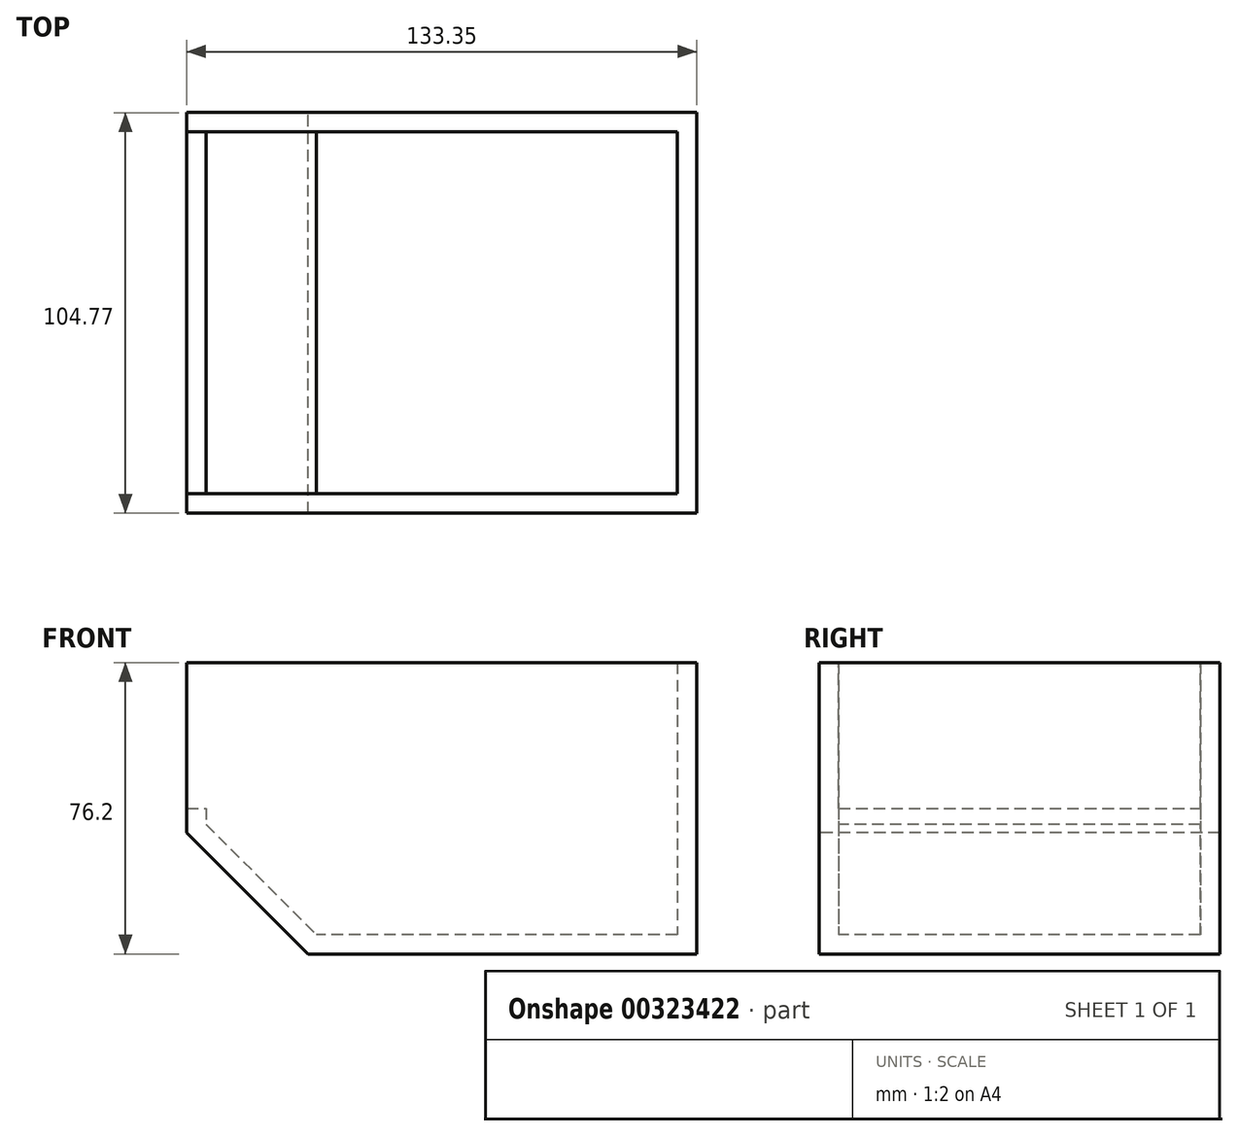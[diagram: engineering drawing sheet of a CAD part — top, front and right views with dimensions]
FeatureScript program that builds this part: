
annotation { "Feature Type Name" : "Feature", "Feature Type Description" : "" }
export const myFeature = defineFeature(function(context is Context, id is Id, definition is map)
    precondition{}
    {
        {
            var Q0;
            Q0=qCreatedBy(makeId("Top.planeOp"),FACE);
            var sketch = newSketch(context, id + "F0", { "sketchPlane" : qUnion([Q0])});
            skLineSegment(sketch, "E0", {"start": v(0, 0) * mm, "end": v(0, 104.78) * mm});
            skLineSegment(sketch, "E1", {"start": v(0, 104.78) * mm, "end": v(133.35, 104.78) * mm});
            skLineSegment(sketch, "E2", {"start": v(133.35, 104.78) * mm, "end": v(133.35, 0) * mm});
            skLineSegment(sketch, "E3", {"start": v(133.35, 0) * mm, "end": v(0, 0) * mm});
            skSolve(sketch);
        }
        {
            var Q0;
            Q0=makeQuery(id+"F0.imprint","IMPRINT",FACE,{"disambiguationData":[TD([[makeQuery(id+"F0.imprint","IMPRINT",EDGE,{"derivedFrom":sQuery(id+"F0.wireOp",EDGE,"E0")}),-1.0]])]});
            extrude(context, id + "F1", {"entities" : qUnion([Q0]), "depth" : 76.2 * mm});
        }
        {
            var Q0;
            Q0=makeQuery(id+"F1.opExtrude","CAP_EDGE",EDGE,{"disambiguationData":[OSD([sQuery(id+"F0.wireOp",EDGE,"E0")])],"isStart":true});
            chamfer(context, id + "F2", {"entities" : qUnion([Q0]), "width" : 31.75 * mm, "tangentPropagation" : true});
        }
        {
            var Q0;
            Q0=makeQuery(id+"F1.opExtrude","CAP_FACE",FACE,{"disambiguationData":[OSD([sQuery(id+"F0.wireOp",EDGE,"E0"),sQuery(id+"F0.wireOp",EDGE,"E1"),sQuery(id+"F0.wireOp",EDGE,"E2"),sQuery(id+"F0.wireOp",EDGE,"E3")])],"isStart":false});
            shell(context, id + "F3", {"entities" : qUnion([Q0]), "thickness" : 5.08 * mm});
        }
        {
            var Q0;
            {var subQ0=sQuery(id+"F0.wireOp",EDGE,"E0");Q0=makeQuery(id+"F3.opShell","OFFSET_FACE",FACE,{"disambiguationData":[OSD([subQ0]),TDD([makeQuery(id+"F1.opExtrude","SWEPT_FACE",FACE,{"disambiguationData":[OSD([subQ0])]})])]});}
            var sketch = newSketch(context, id + "F4", { "sketchPlane" : qUnion([Q0])});
            skLineSegment(sketch, "E4.bottom", {"start": v(5.08, 76.2) * mm, "end": v(99.7, 76.2) * mm});
            skLineSegment(sketch, "E4.top", {"start": v(5.08, 38.1) * mm, "end": v(99.7, 38.1) * mm});
            skLineSegment(sketch, "E4.left", {"start": v(5.08, 76.2) * mm, "end": v(5.08, 38.1) * mm});
            skLineSegment(sketch, "E4.right", {"start": v(99.7, 76.2) * mm, "end": v(99.7, 38.1) * mm});
            skSolve(sketch);
        }
        {
            var Q0;
            Q0=makeQuery(id+"F4.imprint","IMPRINT",FACE,{"disambiguationData":[TD([[makeQuery(id+"F4.imprint","IMPRINT",EDGE,{"derivedFrom":sQuery(id+"F4.wireOp",EDGE,"E4.bottom")}),-1.0]])]});
            extrude(context, id + "F5", {"entities" : qUnion([Q0]), "operationType" : NewBodyOperationType.REMOVE, "oppositeDirection" : true, "depth" : 25.4 * mm});
        }
    });
